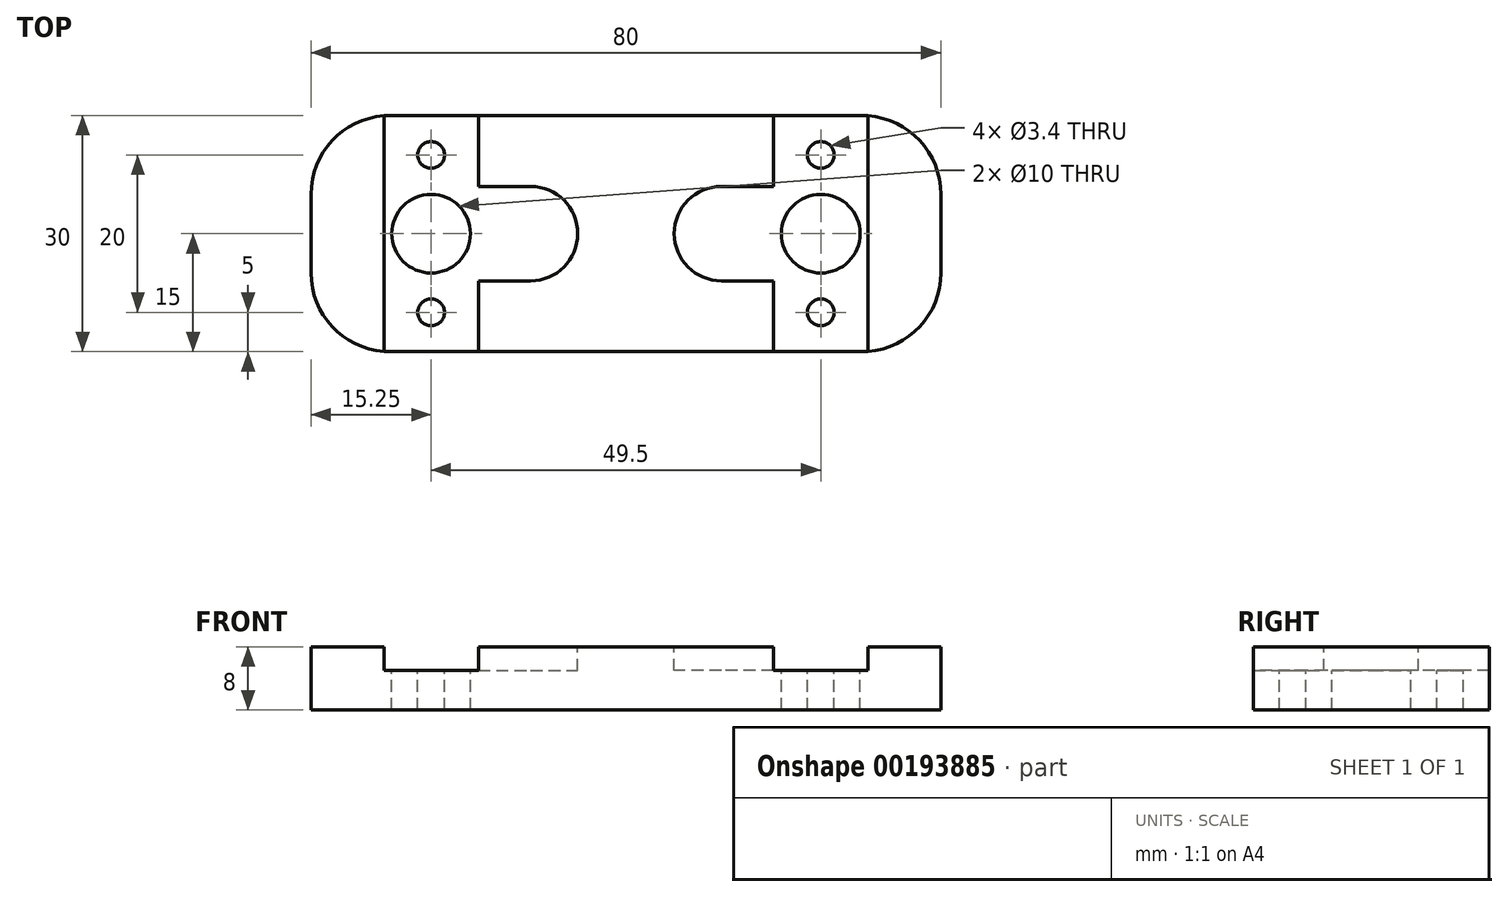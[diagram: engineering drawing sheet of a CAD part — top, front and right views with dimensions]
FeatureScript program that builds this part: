
annotation { "Feature Type Name" : "Feature", "Feature Type Description" : "" }
export const myFeature = defineFeature(function(context is Context, id is Id, definition is map)
    precondition{}
    {
        {
            var Q0;
            Q0=qCreatedBy(makeId("Top.planeOp"),FACE);
            var sketch = newSketch(context, id + "F0", { "sketchPlane" : qUnion([Q0])});
            skLineSegment(sketch, "E0.bottom", {"start": v(40, -15) * mm, "end": v(-40, -15) * mm});
            skLineSegment(sketch, "E0.top", {"start": v(40, 15) * mm, "end": v(-40, 15) * mm});
            skLineSegment(sketch, "E0.left", {"start": v(40, -15) * mm, "end": v(40, 15) * mm});
            skLineSegment(sketch, "E0.right", {"start": v(-40, -15) * mm, "end": v(-40, 15) * mm});
            skPoint(sketch, "E0.middle", {"position": v(0, 0) * mm});
            skSolve(sketch);
        }
        {
            var Q0;
            Q0 = qSketchRegion(id + "F0", true);
            extrude(context, id + "F1", {"entities" : qUnion([Q0]), "endBound" : BoundingType.SYMMETRIC, "depth" : 8 * mm});
        }
        {
            var Q0;
            Q0=makeQuery(id+"F1.opExtrude","CAP_FACE",FACE,{"disambiguationData":[OSD([sQuery(id+"F0.wireOp",EDGE,"E0.bottom"),sQuery(id+"F0.wireOp",EDGE,"E0.top"),sQuery(id+"F0.wireOp",EDGE,"E0.left"),sQuery(id+"F0.wireOp",EDGE,"E0.right")])],"isStart":false});
            var sketch = newSketch(context, id + "F2", { "sketchPlane" : qUnion([Q0])});
            skLineSegment(sketch, "E1", {"start": v(-30.75, 15) * mm, "end": v(-18.75, 15) * mm});
            skLineSegment(sketch, "E2", {"start": v(-18.75, 15) * mm, "end": v(-18.75, 6) * mm});
            skLineSegment(sketch, "E3", {"start": v(-18.75, 6) * mm, "end": v(-12.12, 6) * mm});
            skLineSegment(sketch, "E4", {"start": v(-30.75, 15) * mm, "end": v(-30.75, -15) * mm});
            skLineSegment(sketch, "E5", {"start": v(-30.75, -15) * mm, "end": v(-18.75, -15) * mm});
            skLineSegment(sketch, "E6", {"start": v(-18.75, -15) * mm, "end": v(-18.75, -6) * mm});
            skLineSegment(sketch, "E7", {"start": v(-18.75, -6) * mm, "end": v(-12.12, -6) * mm});
            skLineSegment(sketch, "E8.0", {"start": v(-40, -15) * mm, "end": v(-40, 15) * mm});
            skArc(sketch, "E9", {"start": v(-12.12, -6) * mm, "mid": v(-6.12, 0) * mm, "end": v(-12.12, 6) * mm});
            skLineSegment(sketch, "E10.left", {"start": v(-30.75, 15) * mm, "end": v(-30.75, 7.6) * mm});
            skLineSegment(sketch, "E11.MirrorCS", {"start": v(30.75, 15) * mm, "end": v(30.75, -15) * mm});
            skLineSegment(sketch, "E12.MirrorCS", {"start": v(30.75, 15) * mm, "end": v(18.75, 15) * mm});
            skLineSegment(sketch, "E13.MirrorCS", {"start": v(18.75, 15) * mm, "end": v(18.75, 6) * mm});
            skLineSegment(sketch, "E14.MirrorCS", {"start": v(18.75, 6) * mm, "end": v(12.12, 6) * mm});
            skArc(sketch, "E15.MirrorCS", {"start": v(12.12, -6) * mm, "mid": v(6.12, 0) * mm, "end": v(12.12, 6) * mm});
            skLineSegment(sketch, "E16.MirrorCS", {"start": v(18.75, -6) * mm, "end": v(12.12, -6) * mm});
            skLineSegment(sketch, "E17.MirrorCS", {"start": v(18.75, -15) * mm, "end": v(18.75, -6) * mm});
            skLineSegment(sketch, "E18.MirrorCS", {"start": v(30.75, -15) * mm, "end": v(18.75, -15) * mm});
            skSolve(sketch);
        }
        {
            var Q0;
            Q0 = qSketchRegion(id + "F2", true);
            extrude(context, id + "F3", {"entities" : qUnion([Q0]), "operationType" : NewBodyOperationType.REMOVE, "oppositeDirection" : true, "depth" : 3 * mm});
        }
        {
            var Q0;
            Q0=makeQuery(id+"F3.boolean.opBoolean","COPY",FACE,{"derivedFrom":makeQuery(id+"F3.opExtrude","CAP_FACE",FACE,{"disambiguationData":[OSD([sQuery(id+"F2.wireOp",EDGE,"E1"),sQuery(id+"F2.wireOp",EDGE,"E2"),sQuery(id+"F2.wireOp",EDGE,"E3"),sQuery(id+"F2.wireOp",EDGE,"E4"),sQuery(id+"F2.wireOp",EDGE,"E5"),sQuery(id+"F2.wireOp",EDGE,"E6"),sQuery(id+"F2.wireOp",EDGE,"E7"),sQuery(id+"F2.wireOp",EDGE,"E9"),sQuery(id+"F2.wireOp",EDGE,"E10.left")])],"isStart":false})});
            var sketch = newSketch(context, id + "F4", { "sketchPlane" : qUnion([Q0])});
            skCircle(sketch, "E19", {"center": v(-24.75, 0) * mm, "radius": 5 * mm});
            skCircle(sketch, "E20", {"center": v(-24.75, 10) * mm, "radius": 1.7 * mm});
            skCircle(sketch, "E21", {"center": v(-24.75, -10) * mm, "radius": 1.7 * mm});
            skLineSegment(sketch, "E22.0", {"start": v(-30.75, 15) * mm, "end": v(-30.75, -15) * mm});
            skCircle(sketch, "E23.MirrorC", {"center": v(24.75, 10) * mm, "radius": 1.7 * mm});
            skCircle(sketch, "E24.MirrorC", {"center": v(24.75, 0) * mm, "radius": 5 * mm});
            skCircle(sketch, "E25.MirrorC", {"center": v(24.75, -10) * mm, "radius": 1.7 * mm});
            skSolve(sketch);
        }
        {
            var Q0;
            Q0 = qSketchRegion(id + "F4", true);
            extrude(context, id + "F5", {"entities" : qUnion([Q0]), "operationType" : NewBodyOperationType.REMOVE, "endBound" : BoundingType.THROUGH_ALL, "oppositeDirection" : true, "depth" : 25 * mm});
        }
        {
            var Q0;
            Q0=makeQuery(id+"F1.opExtrude","SWEPT_EDGE",EDGE,{"disambiguationData":[OSD([sQuery(id+"F0.wireOp",EDGE,"E0.top"),sQuery(id+"F0.wireOp",EDGE,"E0.right")])]});
            var Q1;
            Q1=makeQuery(id+"F1.opExtrude","SWEPT_EDGE",EDGE,{"disambiguationData":[OSD([sQuery(id+"F0.wireOp",EDGE,"E0.bottom"),sQuery(id+"F0.wireOp",EDGE,"E0.right")])]});
            var Q2;
            Q2=makeQuery(id+"F1.opExtrude","SWEPT_EDGE",EDGE,{"disambiguationData":[OSD([sQuery(id+"F0.wireOp",EDGE,"E0.top"),sQuery(id+"F0.wireOp",EDGE,"E0.left")])]});
            var Q3;
            Q3=makeQuery(id+"F1.opExtrude","SWEPT_EDGE",EDGE,{"disambiguationData":[OSD([sQuery(id+"F0.wireOp",EDGE,"E0.bottom"),sQuery(id+"F0.wireOp",EDGE,"E0.left")])]});
            fillet(context, id + "F6", {"entities" : qUnion([Q0, Q1, Q2, Q3]), "radius" : 10 * mm, "tangentPropagation" : true, "allowEdgeOverflow" : false});
        }
    });
